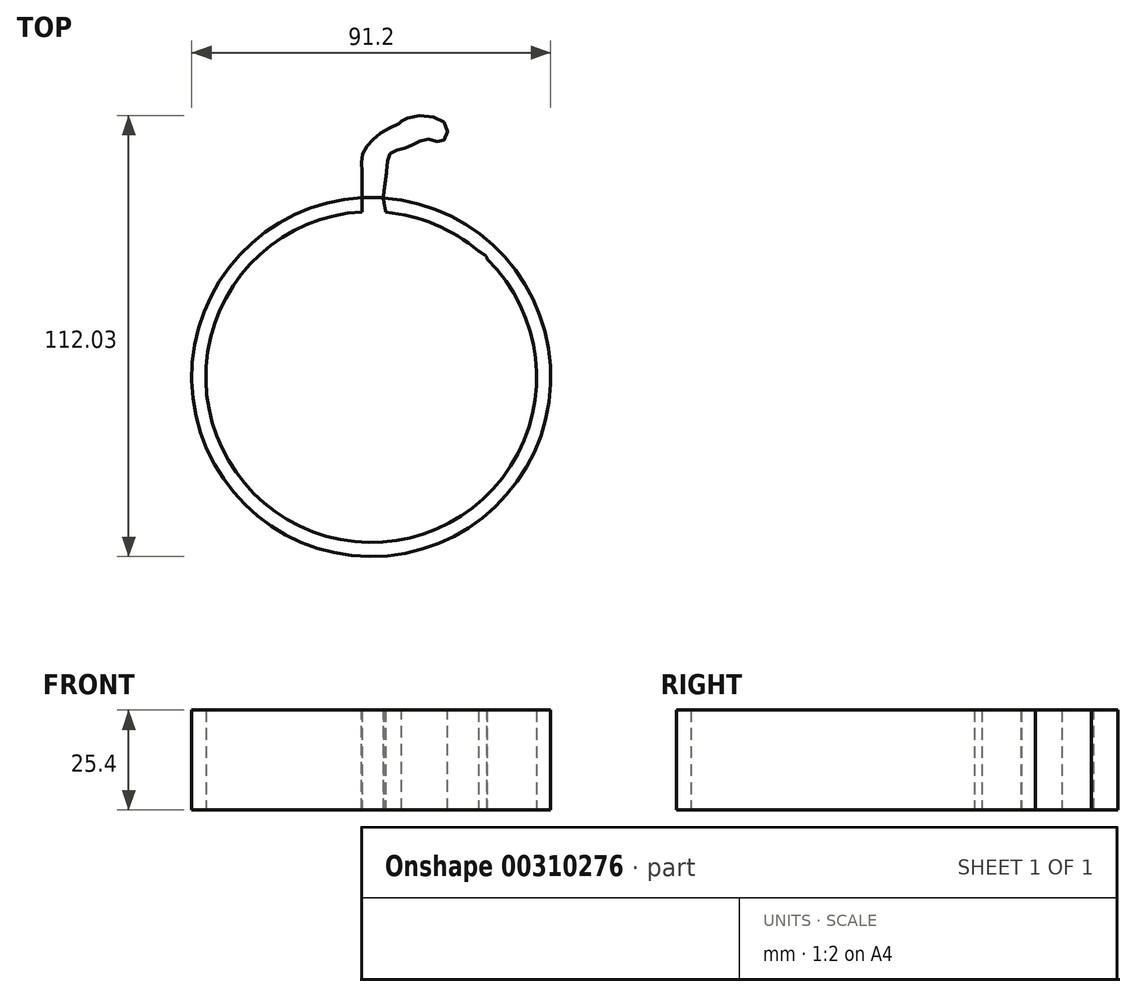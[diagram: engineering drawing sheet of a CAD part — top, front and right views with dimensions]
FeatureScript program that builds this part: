
annotation { "Feature Type Name" : "Feature", "Feature Type Description" : "" }
export const myFeature = defineFeature(function(context is Context, id is Id, definition is map)
    precondition{}
    {
        {
            var Q0;
            Q0=qCreatedBy(makeId("Top.planeOp"),FACE);
            var sketch = newSketch(context, id + "F0", { "sketchPlane" : qUnion([Q0])});
            skCircle(sketch, "E0", {"center": v(0, 0) * mm, "radius": 45.6 * mm});
            skFitSpline(sketch, "E1", {"points": [v(-24.1, 30.47) * mm, v(-22.84, 29.04) * mm, v(-20.7, 27.25) * mm, v(-17.67, 26.36) * mm, v(-17.84, 26.36) * mm, v(-14.1, 25.83) * mm, v(-9.8, 25.11) * mm, v(-5.7, 25.11) * mm, v(-2.3, 25.29) * mm, v(0, 25.25) * mm, v(4.48, 25.11) * mm, v(9.65, 25.65) * mm, v(14.47, 27.79) * mm, v(14.47, 27.79) * mm, v(18.22, 29.22) * mm, v(20.54, 30.47) * mm, v(21.8, 31.54) * mm, v(23.22, 33.68) * mm], "startDerivative": vector(25.65, -28.43) * mm, "endDerivative": vector(22.81, 41.45) * mm});
            skFitSpline(sketch, "E2", {"points": [v(0, 26.27) * mm, v(-0.1, 26.08) * mm, v(-0.23, 25.9) * mm, v(-0.23, 25.9) * mm, v(-0.33, 25.72) * mm, v(-0.34, 25.72) * mm, v(-0.62, 25.27) * mm], "startDerivative": vector(-0.39, -0.86) * mm, "endDerivative": vector(-1.18, -2.02) * mm});
            skCircle(sketch, "E3", {"center": v(0, 0) * mm, "radius": 42.02 * mm});
            skFitSpline(sketch, "E4", {"points": [v(8.88, 21.84) * mm, v(8.25, 21.87) * mm], "startDerivative": vector(-0.63, 0.04) * mm, "endDerivative": vector(-0.63, 0.04) * mm});
            skFitSpline(sketch, "E5", {"points": [v(-23.67, 30) * mm, v(-27.2, 26.06) * mm, v(-20.65, 21.42) * mm, v(-5.93, 20.6) * mm, v(11.8, 20.6) * mm, v(23.26, 25.95) * mm, v(29.42, 30) * mm, v(23.22, 33.68) * mm], "startDerivative": vector(-52.68, -36.55) * mm, "endDerivative": vector(-76.93, 30.2) * mm});
            skFitSpline(sketch, "E6", {"points": [v(-2.3, 25.29) * mm, v(-2.3, 39.42) * mm, v(-2.3, 52.24) * mm], "startDerivative": vector(0, 27.93) * mm, "endDerivative": vector(0, 25.96) * mm});
            skFitSpline(sketch, "E7", {"points": [v(-2.3, 52.24) * mm, v(-2.3, 56.33) * mm, v(0, 59.88) * mm, v(3.9, 62.88) * mm, v(7.71, 64.78) * mm, v(7.71, 65.06) * mm, v(12.62, 66.42) * mm, v(19.17, 63.7) * mm, v(18.07, 59.88) * mm, v(14.53, 60.42) * mm, v(10.71, 59.06) * mm, v(7.71, 57.97) * mm, v(4.71, 56.6) * mm, v(3.9, 52.24) * mm, v(3.14, 45.49) * mm, v(3.69, 41.86) * mm, v(3.9, 33.97) * mm, v(3.9, 28.79) * mm, v(4.48, 26.27) * mm, v(4.48, 25.11) * mm], "startDerivative": vector(-10.27, 78.49) * mm, "endDerivative": vector(-3.58, -37.64) * mm});
            skFitSpline(sketch, "E8", {"points": [v(20.97, 25.61) * mm, v(21.2, 25.47) * mm], "startDerivative": vector(0.23, -0.14) * mm, "endDerivative": vector(0.23, -0.14) * mm});
            skFitSpline(sketch, "E9", {"points": [v(3.9, 52.24) * mm, v(5.36, 48.8) * mm, v(6.82, 46.77) * mm, v(8.34, 44.83) * mm], "startDerivative": vector(3.63, -9.78) * mm, "endDerivative": vector(4.9, -6.45) * mm});
            skFitSpline(sketch, "E10", {"points": [v(-2.3, 52.24) * mm, v(-5.12, 49.03) * mm, v(-5.9, 47.45) * mm, v(-7.55, 44.97) * mm], "startDerivative": vector(-8.33, -8.66) * mm, "endDerivative": vector(-5.63, -7.9) * mm});
            skSolve(sketch);
        }
        {
            var Q0;
            {var subQ0=sQuery(id+"F0.wireOp",EDGE,"E6");var subQ1=sQuery(id+"F0.wireOp",EDGE,"E1");var subQ2=makeQuery(id+"F0.imprint","INTERSECT",VERTEX,{"derivedFrom":[subQ1,subQ0]});Q0=makeQuery(id+"F0.imprint","IMPRINT",FACE,{"disambiguationData":[TD([[makeQuery(id+"F0.imprint","IMPRINT",EDGE,{"disambiguationData":[TD([[subQ2,1.0]])],"derivedFrom":subQ1}),1.0]])]});}
            var Q1;
            {var subQ0=sQuery(id+"F0.wireOp",EDGE,"E1");var subQ1=makeQuery(id+"F0.imprint","IMPRINT",VERTEX,{"derivedFrom":subQ0});Q1=makeQuery(id+"F0.imprint","IMPRINT",FACE,{"disambiguationData":[TD([[makeQuery(id+"F0.imprint","IMPRINT",EDGE,{"disambiguationData":[TD([[subQ1,1.0]])],"derivedFrom":subQ0}),1.0]])]});}
            var Q2;
            {var subQ0=sQuery(id+"F0.wireOp",EDGE,"E5");var subQ1=sQuery(id+"F0.wireOp",EDGE,"E1");var subQ2=makeQuery(id+"F0.imprint","INTERSECT",VERTEX,{"disambiguationData":[OD(0.0)],"derivedFrom":[subQ1,subQ0]});Q2=makeQuery(id+"F0.imprint","IMPRINT",FACE,{"disambiguationData":[TD([[makeQuery(id+"F0.imprint","IMPRINT",EDGE,{"disambiguationData":[TD([[subQ2,1.0]])],"derivedFrom":subQ1}),1.0]])]});}
            var Q3;
            {var subQ0=sQuery(id+"F0.wireOp",EDGE,"E6");var subQ1=sQuery(id+"F0.wireOp",EDGE,"E0");var subQ2=makeQuery(id+"F0.imprint","INTERSECT",VERTEX,{"derivedFrom":[subQ1,subQ0]});Q3=makeQuery(id+"F0.imprint","IMPRINT",FACE,{"disambiguationData":[TD([[makeQuery(id+"F0.imprint","IMPRINT",EDGE,{"disambiguationData":[TD([[subQ2,1.0]])],"derivedFrom":subQ1}),-1.0]])]});}
            var Q4;
            {var subQ3=sQuery(id+"F0.wireOp",EDGE,"E6");var subQ8=sQuery(id+"F0.wireOp",EDGE,"E0");var subQ9=makeQuery(id+"F0.imprint","INTERSECT",VERTEX,{"derivedFrom":[subQ8,subQ3]});Q4=makeQuery(id+"F0.imprint","IMPRINT",FACE,{"disambiguationData":[TD([[makeQuery(id+"F0.imprint","IMPRINT",EDGE,{"disambiguationData":[TD([[subQ9,-1.0]])],"derivedFrom":subQ8}),1.0]])]});}
            extrude(context, id + "F1", {"entities" : qUnion([Q0, Q1, Q2, Q3, Q4]), "depth" : 25.4 * mm});
        }
    });
